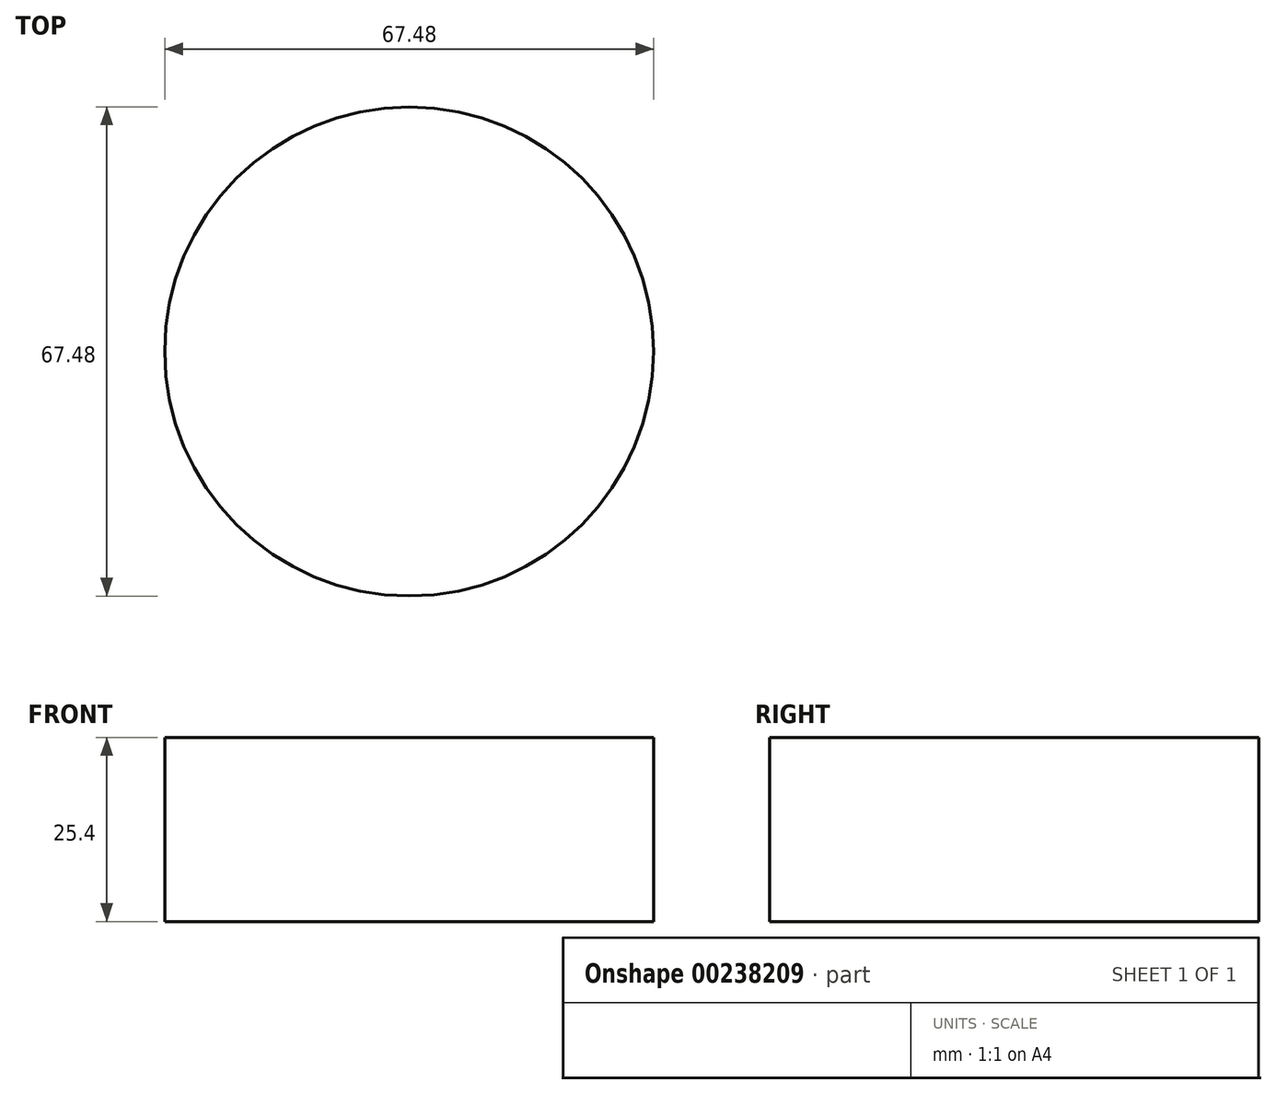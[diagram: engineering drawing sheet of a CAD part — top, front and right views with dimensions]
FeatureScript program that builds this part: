
annotation { "Feature Type Name" : "Feature", "Feature Type Description" : "" }
export const myFeature = defineFeature(function(context is Context, id is Id, definition is map)
    precondition{}
    {
        {
            var Q0;
            Q0=qCreatedBy(makeId("Top.planeOp"),FACE);
            var sketch = newSketch(context, id + "F1", { "sketchPlane" : qUnion([Q0])});
            skCircle(sketch, "E0", {"center": v(0, 0) * mm, "radius": 33.74 * mm});
            skSolve(sketch);
        }
        {
            var Q0;
            Q0=makeQuery(id+"F1.imprint","IMPRINT",FACE,{"disambiguationData":[TD([[makeQuery(id+"F1.imprint","IMPRINT",EDGE,{"derivedFrom":sQuery(id+"F1.wireOp",EDGE,"E0")}),1.0]])]});
            var sketch = newSketch(context, id + "F0", { "sketchPlane" : qUnion([Q0])});
            skSolve(sketch);
        }
        {
            var Q0;
            Q0 = qSketchRegion(id + "F0", true);
            var Q1;
            Q1=makeQuery(id+"F1.imprint","IMPRINT",FACE,{"disambiguationData":[TD([[makeQuery(id+"F1.imprint","IMPRINT",EDGE,{"derivedFrom":sQuery(id+"F1.wireOp",EDGE,"E0")}),1.0]])]});
            extrude(context, id + "F2", {"entities" : qUnion([Q0, Q1]), "depth" : 25.4 * mm});
        }
    });
